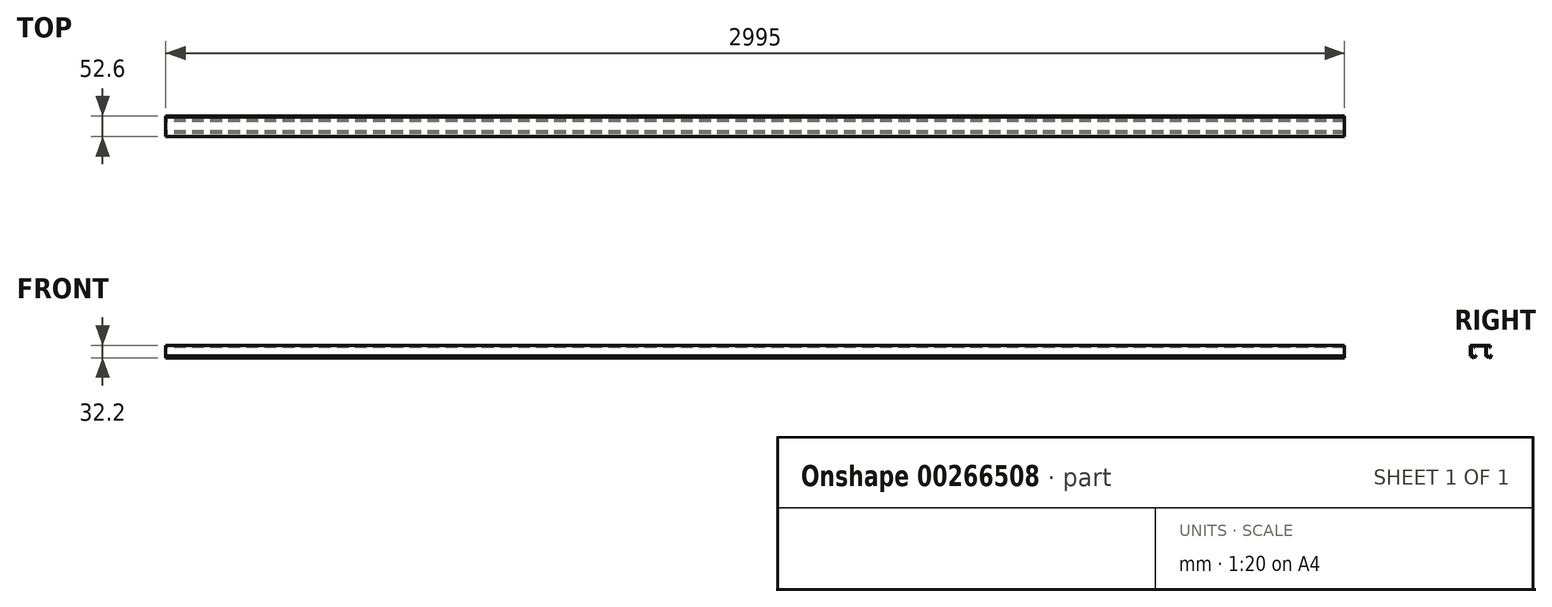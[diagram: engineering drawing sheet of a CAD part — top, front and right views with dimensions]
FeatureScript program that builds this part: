
annotation { "Feature Type Name" : "Feature", "Feature Type Description" : "" }
export const myFeature = defineFeature(function(context is Context, id is Id, definition is map)
    precondition{}
    {
        {
            var Q0;
            Q0=qCreatedBy(makeId("Right.planeOp"),FACE);
            var sketch = newSketch(context, id + "F0", { "sketchPlane" : qUnion([Q0])});
            skLineSegment(sketch, "E0", {"start": v(-36, -23.6) * mm, "end": v(-36, -25.6) * mm});
            skLineSegment(sketch, "E1", {"start": v(-36, -25.6) * mm, "end": v(-42, -29.8) * mm});
            skLineSegment(sketch, "E2", {"start": v(-36, -23.6) * mm, "end": v(-38, -23.6) * mm});
            skLineSegment(sketch, "E3", {"start": v(-38, -23.6) * mm, "end": v(-38, -24.56) * mm});
            skLineSegment(sketch, "E4", {"start": v(-38, -24.56) * mm, "end": v(-42, -27.36) * mm});
            skLineSegment(sketch, "E5", {"start": v(-42, -29.8) * mm, "end": v(-50, -24.2) * mm});
            skLineSegment(sketch, "E6", {"start": v(-50, -24.2) * mm, "end": v(-50, 2.4) * mm});
            skLineSegment(sketch, "E7", {"start": v(-42, -27.36) * mm, "end": v(-48, -23.16) * mm});
            skLineSegment(sketch, "E8", {"start": v(-48, -23.16) * mm, "end": v(-48, 0.4) * mm});
            skLineSegment(sketch, "E9", {"start": v(-50, 2.4) * mm, "end": v(0, 2.4) * mm});
            skLineSegment(sketch, "E10", {"start": v(-48, 0.4) * mm, "end": v(-40.6, 0.4) * mm});
            skLineSegment(sketch, "E11", {"start": v(-40.6, 0.4) * mm, "end": v(-40.6, -2.6) * mm});
            skLineSegment(sketch, "E12", {"start": v(-40.6, -2.6) * mm, "end": v(-38.6, -2.6) * mm});
            skLineSegment(sketch, "E13", {"start": v(-38.6, -2.6) * mm, "end": v(-38.6, 0.4) * mm});
            skLineSegment(sketch, "E14", {"start": v(-38.6, 0.4) * mm, "end": v(-11.4, 0.4) * mm});
            skLineSegment(sketch, "E15", {"start": v(-11.4, 0.4) * mm, "end": v(-11.4, -24.2) * mm});
            skLineSegment(sketch, "E16", {"start": v(-11.4, -24.2) * mm, "end": v(-3.4, -29.8) * mm});
            skLineSegment(sketch, "E17", {"start": v(-3.4, -29.8) * mm, "end": v(2.6, -25.6) * mm});
            skLineSegment(sketch, "E18", {"start": v(2.6, -25.6) * mm, "end": v(2.6, -23.6) * mm});
            skLineSegment(sketch, "E19", {"start": v(2.6, -23.6) * mm, "end": v(0.6, -23.6) * mm});
            skLineSegment(sketch, "E20", {"start": v(0, 2.4) * mm, "end": v(0, -2.6) * mm});
            skLineSegment(sketch, "E21", {"start": v(0, -2.6) * mm, "end": v(-2, -2.6) * mm});
            skLineSegment(sketch, "E22", {"start": v(-2, -2.6) * mm, "end": v(-2, 0.4) * mm});
            skLineSegment(sketch, "E23", {"start": v(-2, 0.4) * mm, "end": v(-9.4, 0.4) * mm});
            skLineSegment(sketch, "E24", {"start": v(-9.4, 0.4) * mm, "end": v(-9.4, -23.16) * mm});
            skLineSegment(sketch, "E25", {"start": v(-42, -27.36) * mm, "end": v(-42, 26.68) * mm, "construction": true});
            skLineSegment(sketch, "E26", {"start": v(-3.4, -29.8) * mm, "end": v(-3.4, 24.67) * mm, "construction": true});
            skLineSegment(sketch, "E27", {"start": v(-40.6, -2.6) * mm, "end": v(-42, -2.6) * mm, "construction": true});
            skLineSegment(sketch, "E28", {"start": v(-2, -2.6) * mm, "end": v(-3.4, -2.6) * mm, "construction": true});
            skLineSegment(sketch, "E29", {"start": v(0.6, -24.56) * mm, "end": v(-3.4, -27.36) * mm});
            skLineSegment(sketch, "E30", {"start": v(0.6, -23.6) * mm, "end": v(0.6, -24.56) * mm});
            skLineSegment(sketch, "E31", {"start": v(-3.4, -27.36) * mm, "end": v(-9.4, -23.16) * mm});
            skSolve(sketch);
        }
        {
            var Q0;
            Q0=makeQuery(id+"F0.imprint","IMPRINT",FACE,{"disambiguationData":[TD([[makeQuery(id+"F0.imprint","IMPRINT",EDGE,{"derivedFrom":sQuery(id+"F0.wireOp",EDGE,"E0")}),-1.0]])]});
            extrude(context, id + "F1", {"entities" : qUnion([Q0]), "depth" : 2995 * mm});
        }
    });
